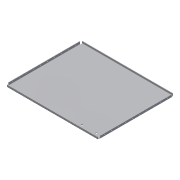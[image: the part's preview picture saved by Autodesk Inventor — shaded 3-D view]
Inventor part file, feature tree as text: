
AUTODESK INVENTOR PART (.ipt)
format: ipt  version: 2016 SP2 (Build 200236200, 236)  size: 195,072 bytes
history: native  units: in
note: dims shown in document units (in); Inventor stores cm internally (conversion verified against a paired STEP export)
features: hole x1, sketch x1, reference x1
ambient origin geometry x8: Origin, YZ Plane, XZ Plane, XY Plane, X Axis, Y Axis, Z Axis, Center Point
bodies: Solid1 (feature_tree)
feature tree (3):
  hole  "Hole1"  [1 undecoded]
  sketch  "Sketch1"  dims[d0=0.2559in d1=0.2362in d2=0.1575in d3=0.0787in d4=90.0deg d5=0.315in d6=0.8108in d7=0.7874in d8=1.122in d9=3.563in]
  reference  "Reference1"
note: 1 required parameter value undecoded (feature->parameter linkage not recoverable at this tier; creation-order binding heuristic only, values carry confidence <= 0.55)
